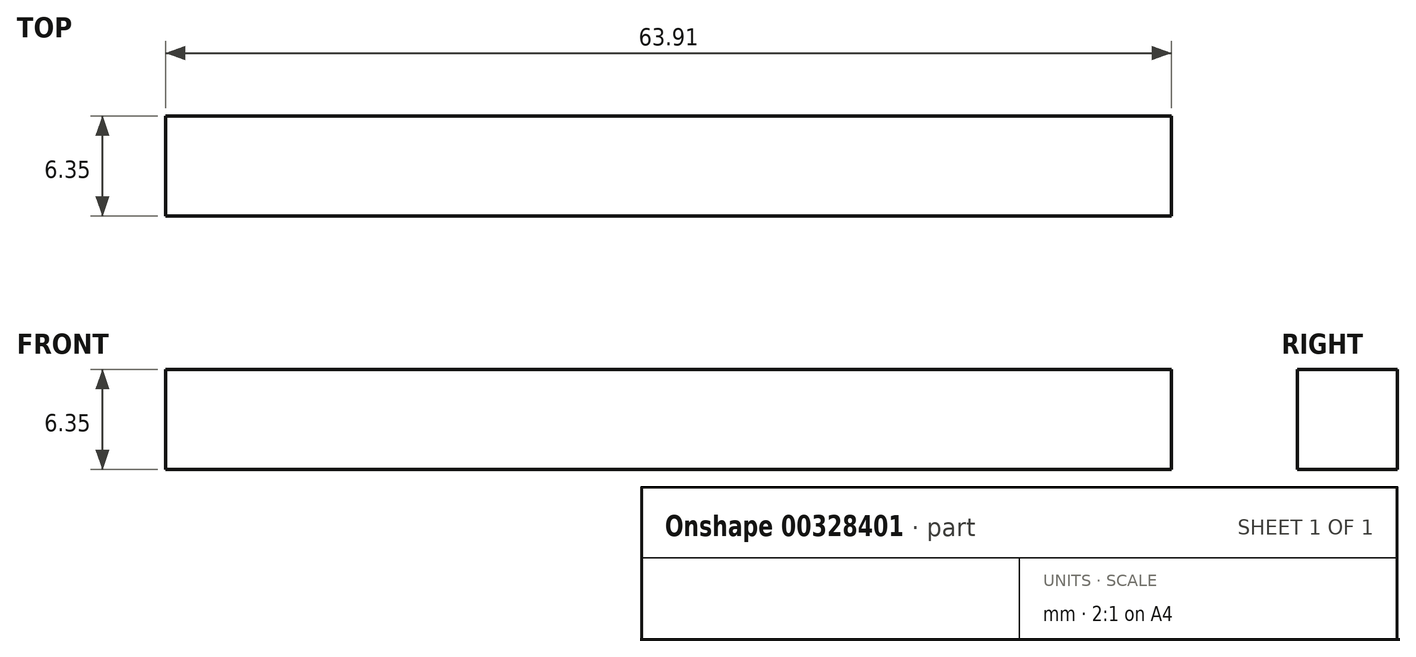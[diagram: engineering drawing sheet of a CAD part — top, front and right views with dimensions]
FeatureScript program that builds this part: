
annotation { "Feature Type Name" : "Feature", "Feature Type Description" : "" }
export const myFeature = defineFeature(function(context is Context, id is Id, definition is map)
    precondition{}
    {
        {
            var Q0;
            Q0=qCreatedBy(makeId("Top.planeOp"),FACE);
            var sketch = newSketch(context, id + "F0", { "sketchPlane" : qUnion([Q0])});
            skLineSegment(sketch, "E0.bottom", {"start": v(0, 0) * mm, "end": v(63.9, 0) * mm});
            skLineSegment(sketch, "E0.top", {"start": v(0, -6.35) * mm, "end": v(63.9, -6.35) * mm});
            skLineSegment(sketch, "E0.left", {"start": v(0, 0) * mm, "end": v(0, -6.35) * mm});
            skLineSegment(sketch, "E0.right", {"start": v(63.9, 0) * mm, "end": v(63.9, -6.35) * mm});
            skSolve(sketch);
        }
        {
            var Q0;
            Q0 = qSketchRegion(id + "F0", true);
            extrude(context, id + "F1", {"entities" : qUnion([Q0]), "depth" : 6.35 * mm});
        }
    });
